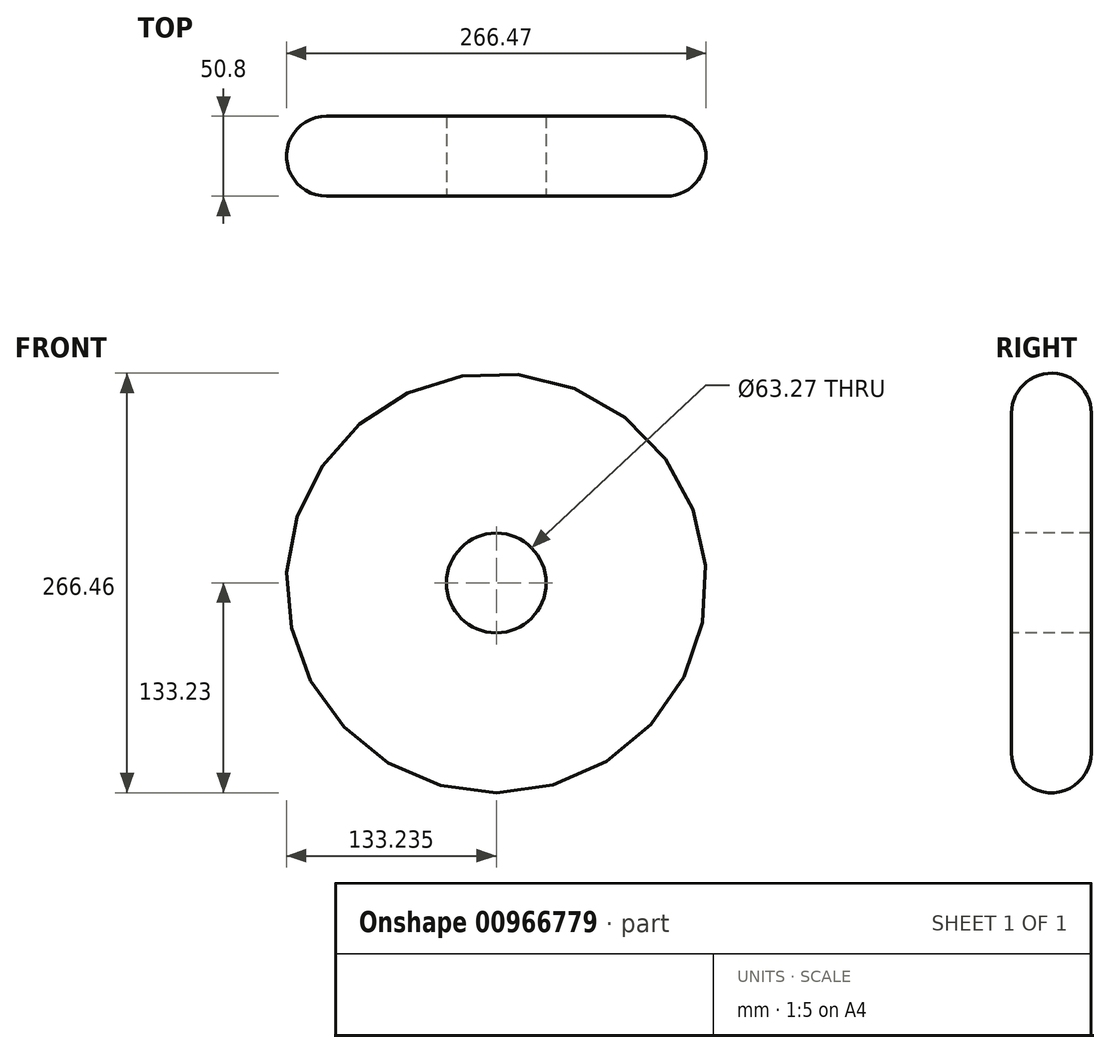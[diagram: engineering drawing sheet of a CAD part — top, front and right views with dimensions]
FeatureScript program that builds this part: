
annotation { "Feature Type Name" : "Feature", "Feature Type Description" : "" }
export const myFeature = defineFeature(function(context is Context, id is Id, definition is map)
    precondition{}
    {
        {
            var Q0;
            Q0=qCreatedBy(makeId("Top.planeOp"),FACE);
            var sketch = newSketch(context, id + "F0", { "sketchPlane" : qUnion([Q0])});
            skLineSegment(sketch, "E0", {"start": v(0, 0) * mm, "end": v(0, 50.8) * mm});
            skLineSegment(sketch, "E1", {"start": v(0, 50.8) * mm, "end": v(76.2, 50.8) * mm});
            skLineSegment(sketch, "E2", {"start": v(76.2, 0) * mm, "end": v(0, 0) * mm});
            skArc(sketch, "E3", {"start": v(76.2, 0) * mm, "mid": v(101.6, 25.4) * mm, "end": v(76.2, 50.8) * mm});
            skPoint(sketch, "E3.centerSnap0", {"position": v(0, 25.4) * mm});
            skLineSegment(sketch, "E4", {"start": v(-31.63, 0) * mm, "end": v(-31.63, 50.8) * mm});
            skSolve(sketch);
        }
        {
            var Q0;
            Q0=makeQuery(id+"F0.imprint","IMPRINT",FACE,{"disambiguationData":[TD([[makeQuery(id+"F0.imprint","IMPRINT",EDGE,{"derivedFrom":sQuery(id+"F0.wireOp",EDGE,"E0")}),-1.0]])]});
            var Q1;
            Q1=sQuery(id+"F0.wireOp",EDGE,"E4");
            revolve(context, id + "F1", {"surfaceOperationType" : NewSurfaceOperationType.NEW, "entities" : qUnion([Q0]), "axis" : qUnion([Q1]), "revolveType" : RevolveType.FULL});
        }
    });
